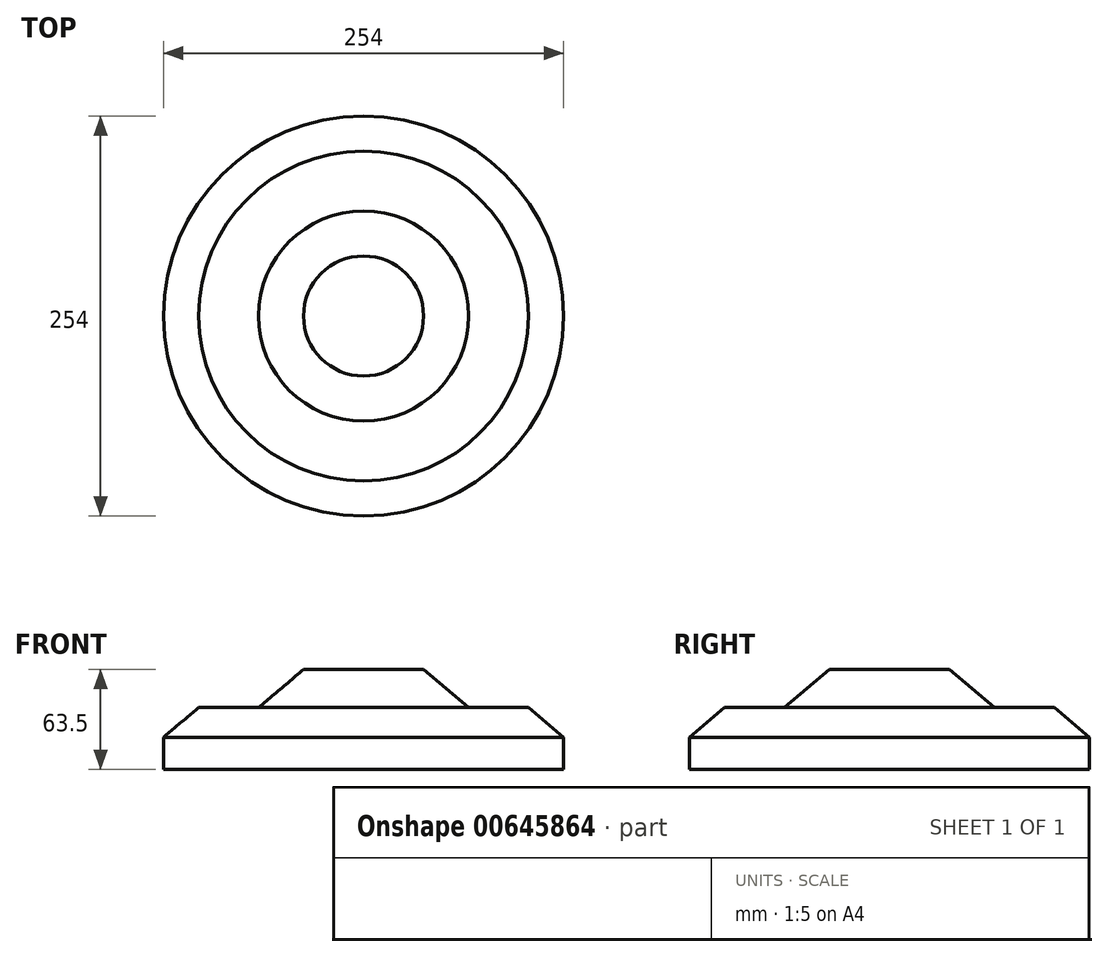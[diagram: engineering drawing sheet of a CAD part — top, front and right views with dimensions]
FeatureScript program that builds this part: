
annotation { "Feature Type Name" : "Feature", "Feature Type Description" : "" }
export const myFeature = defineFeature(function(context is Context, id is Id, definition is map)
    precondition{}
    {
        {
            var Q0;
            Q0=qCreatedBy(makeId("Front.planeOp"),FACE);
            var sketch = newSketch(context, id + "F0", { "sketchPlane" : qUnion([Q0])});
            skLineSegment(sketch, "E0", {"start": v(0, 63.5) * mm, "end": v(38.1, 63.5) * mm});
            skLineSegment(sketch, "E1", {"start": v(38.1, 63.5) * mm, "end": v(66.72, 39.25) * mm});
            skLineSegment(sketch, "E2", {"start": v(66.72, 39.25) * mm, "end": v(104.82, 39.25) * mm});
            skLineSegment(sketch, "E3", {"start": v(104.82, 39.25) * mm, "end": v(127, 20.46) * mm});
            skLineSegment(sketch, "E4", {"start": v(127, 20.46) * mm, "end": v(127, 0) * mm});
            skLineSegment(sketch, "E5", {"start": v(127, 0) * mm, "end": v(0, 0) * mm});
            skLineSegment(sketch, "E6", {"start": v(0, 0) * mm, "end": v(0, 63.5) * mm});
            skSolve(sketch);
        }
        {
            var Q0;
            Q0=makeQuery(id+"F0.imprint","IMPRINT",FACE,{"disambiguationData":[TD([[makeQuery(id+"F0.imprint","IMPRINT",EDGE,{"derivedFrom":sQuery(id+"F0.wireOp",EDGE,"E0")}),-1.0]])]});
            var Q1;
            Q1=sQuery(id+"F0.wireOp",EDGE,"E6");
            revolve(context, id + "F1", {"entities" : qUnion([Q0]), "axis" : qUnion([Q1]), "revolveType" : RevolveType.FULL});
        }
    });
